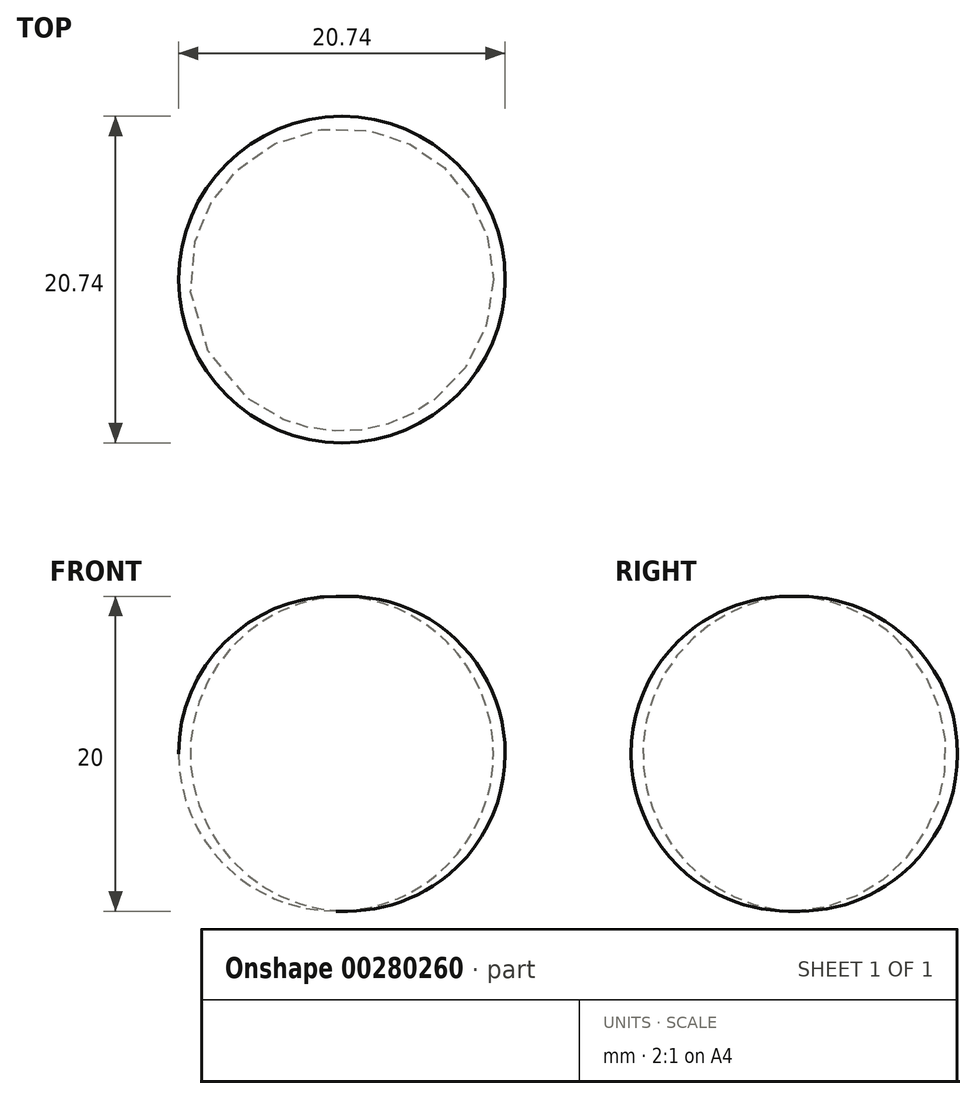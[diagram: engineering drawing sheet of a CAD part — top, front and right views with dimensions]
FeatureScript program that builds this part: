
annotation { "Feature Type Name" : "Feature", "Feature Type Description" : "" }
export const myFeature = defineFeature(function(context is Context, id is Id, definition is map)
    precondition{}
    {
        {
            var Q0;
            Q0=qCreatedBy(makeId("Front.planeOp"),FACE);
            var sketch = newSketch(context, id + "F0", { "sketchPlane" : qUnion([Q0])});
            skLineSegment(sketch, "E0", {"start": v(0, 0) * mm, "end": v(0, 19.99) * mm});
            skArc(sketch, "E1", {"start": v(0, 0) * mm, "mid": v(10.37, 10) * mm, "end": v(0, 19.99) * mm});
            skSolve(sketch);
        }
        {
            var Q0;
            Q0 = qSketchRegion(id + "F0", true);
            var Q1;
            Q1=sQuery(id+"F0.wireOp",EDGE,"E0");
            revolve(context, id + "F1", {"entities" : qUnion([Q0]), "axis" : qUnion([Q1]), "revolveType" : RevolveType.FULL});
        }
    });
